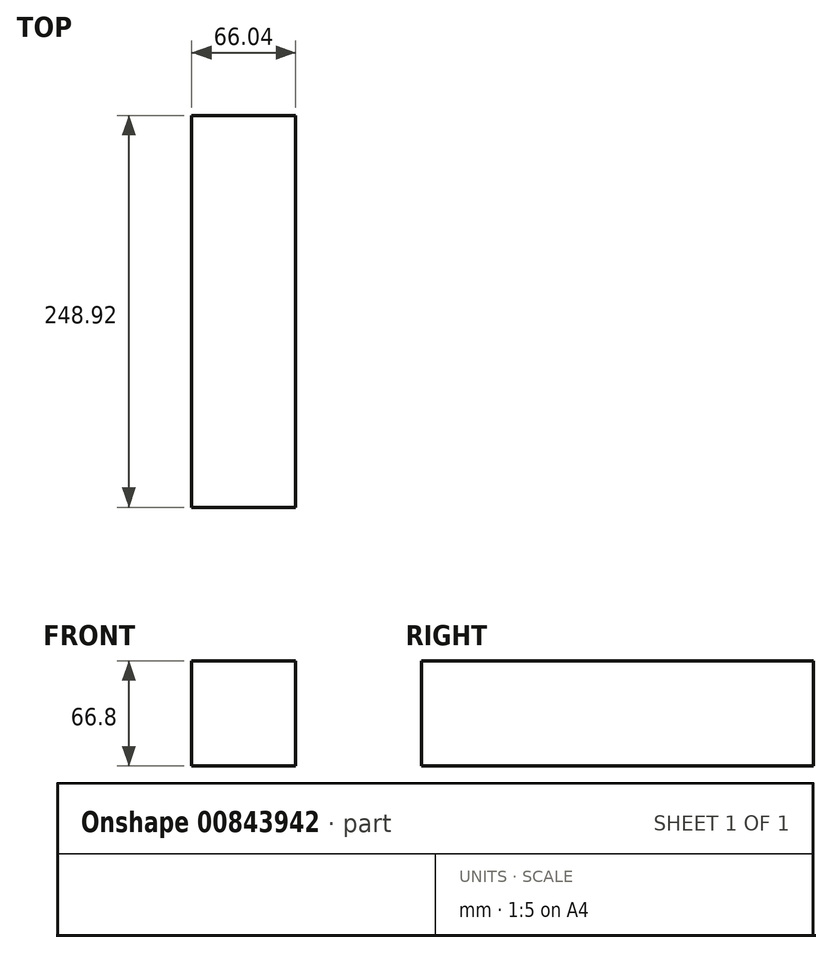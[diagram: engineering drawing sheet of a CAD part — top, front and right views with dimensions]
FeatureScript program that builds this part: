
annotation { "Feature Type Name" : "Feature", "Feature Type Description" : "" }
export const myFeature = defineFeature(function(context is Context, id is Id, definition is map)
    precondition{}
    {
        {
            var Q0;
            Q0=qCreatedBy(makeId("Front.planeOp"),FACE);
            var sketch = newSketch(context, id + "F0", { "sketchPlane" : qUnion([Q0])});
            skLineSegment(sketch, "E0.bottom", {"start": v(-66.04, 66.8) * mm, "end": v(0, 66.8) * mm});
            skLineSegment(sketch, "E0.top", {"start": v(-66.04, 0) * mm, "end": v(0, 0) * mm});
            skLineSegment(sketch, "E0.left", {"start": v(-66.04, 66.8) * mm, "end": v(-66.04, 0) * mm});
            skLineSegment(sketch, "E0.right", {"start": v(0, 66.8) * mm, "end": v(0, 0) * mm});
            skSolve(sketch);
        }
        {
            var Q0;
            Q0=makeQuery(id+"F0.imprint","IMPRINT",FACE,{"disambiguationData":[TD([[makeQuery(id+"F0.imprint","IMPRINT",EDGE,{"derivedFrom":sQuery(id+"F0.wireOp",EDGE,"E0.bottom")}),-1.0]])]});
            extrude(context, id + "F1", {"entities" : qUnion([Q0]), "depth" : 248.92 * mm, "offsetDistance" : 25.4 * mm});
        }
    });
